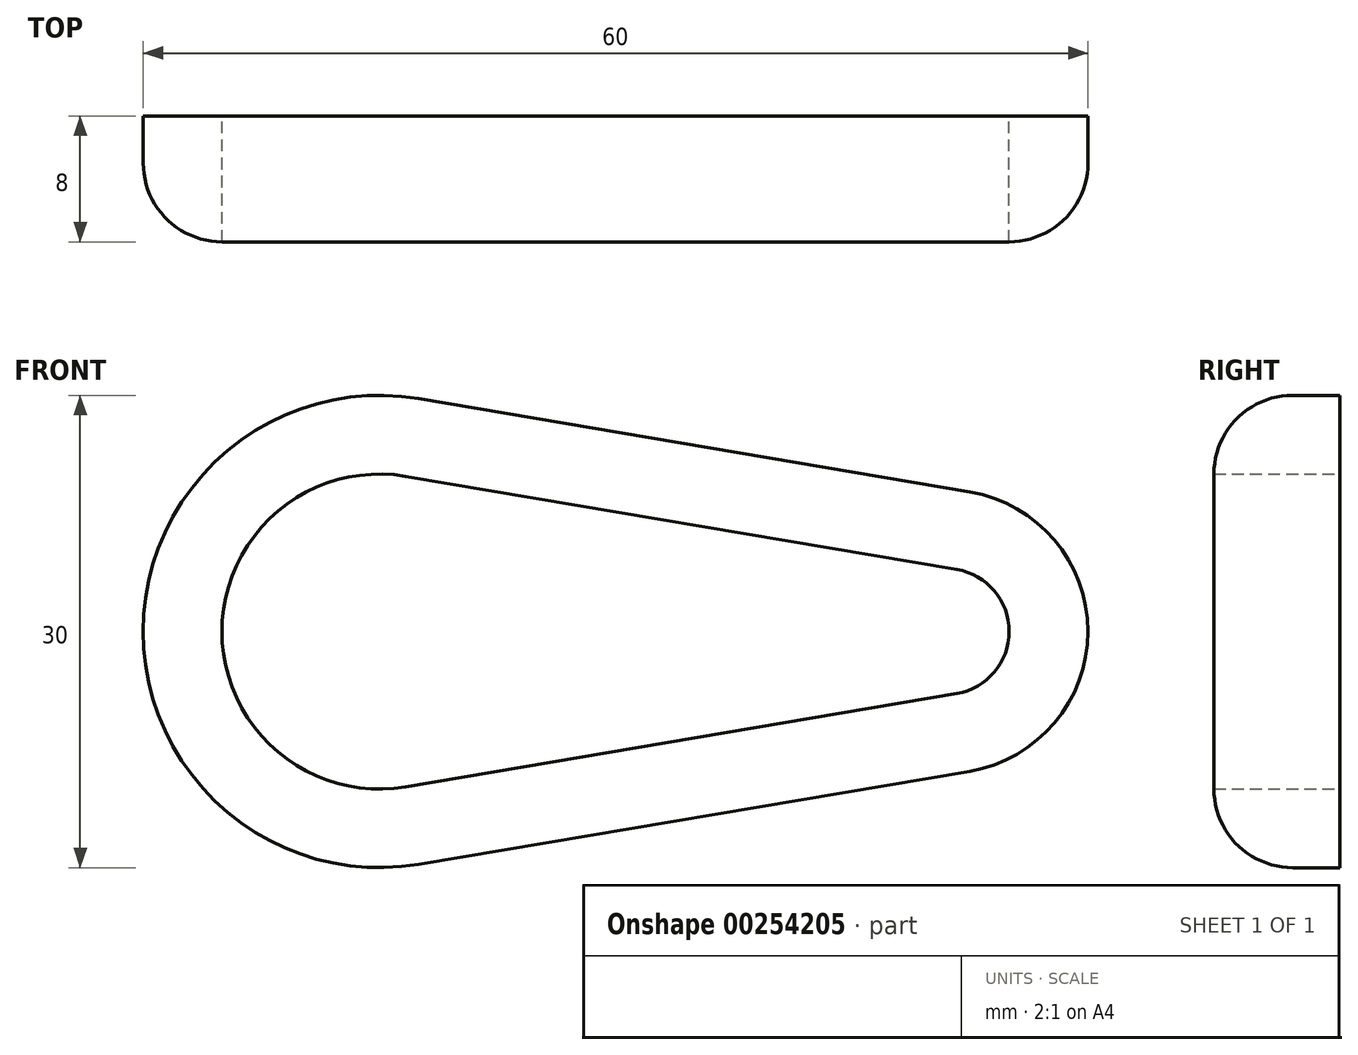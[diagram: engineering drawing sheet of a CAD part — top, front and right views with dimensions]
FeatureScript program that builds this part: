
annotation { "Feature Type Name" : "Feature", "Feature Type Description" : "" }
export const myFeature = defineFeature(function(context is Context, id is Id, definition is map)
    precondition{}
    {
        {
            var Q0;
            Q0=qCreatedBy(makeId("Front.planeOp"),FACE);
            var sketch = newSketch(context, id + "F0", { "sketchPlane" : qUnion([Q0])});
            skCircle(sketch, "E0", {"center": v(-38.66, 0) * mm, "radius": 10 * mm});
            skCircle(sketch, "E1", {"center": v(-2.66, 0) * mm, "radius": 4 * mm});
            skLineSegment(sketch, "E2", {"start": v(-37, 9.86) * mm, "end": v(-2, 3.94) * mm});
            skLineSegment(sketch, "E3", {"start": v(-37, -9.86) * mm, "end": v(-2, -3.94) * mm});
            skCircle(sketch, "E4.0", {"center": v(-38.66, 0) * mm, "radius": 15 * mm});
            skCircle(sketch, "E5.0", {"center": v(-2.66, 0) * mm, "radius": 9 * mm});
            skLineSegment(sketch, "E6", {"start": v(-36.16, 14.8) * mm, "end": v(-1.16, 8.87) * mm});
            skLineSegment(sketch, "E7", {"start": v(-36.16, -14.8) * mm, "end": v(-1.16, -8.87) * mm});
            skSolve(sketch);
        }
        {
            var Q0;
            {var subQ2=sQuery(id+"F0.wireOp",EDGE,"E2");var subQ5=sQuery(id+"F0.wireOp",EDGE,"E0");var subQ8=makeQuery(id+"F0.imprint","INTERSECT",VERTEX,{"derivedFrom":[subQ5,subQ2]});Q0=makeQuery(id+"F0.imprint","IMPRINT",FACE,{"disambiguationData":[TD([[makeQuery(id+"F0.imprint","IMPRINT",EDGE,{"disambiguationData":[TD([[subQ8,-1.0]])],"derivedFrom":subQ5}),-1.0]])]});}
            var Q1;
            {var subQ5=sQuery(id+"F0.wireOp",EDGE,"E6");Q1=makeQuery(id+"F0.imprint","IMPRINT",FACE,{"disambiguationData":[TD([[makeQuery(id+"F0.imprint","IMPRINT",EDGE,{"derivedFrom":subQ5}),-1.0]])]});}
            var Q2;
            {var subQ5=sQuery(id+"F0.wireOp",EDGE,"E7");Q2=makeQuery(id+"F0.imprint","IMPRINT",FACE,{"disambiguationData":[TD([[makeQuery(id+"F0.imprint","IMPRINT",EDGE,{"derivedFrom":subQ5}),1.0]])]});}
            var Q3;
            {var subQ2=sQuery(id+"F0.wireOp",EDGE,"E2");var subQ5=sQuery(id+"F0.wireOp",EDGE,"E1");var subQ8=makeQuery(id+"F0.imprint","INTERSECT",VERTEX,{"derivedFrom":[subQ5,subQ2]});Q3=makeQuery(id+"F0.imprint","IMPRINT",FACE,{"disambiguationData":[TD([[makeQuery(id+"F0.imprint","IMPRINT",EDGE,{"disambiguationData":[TD([[subQ8,1.0]])],"derivedFrom":subQ5}),-1.0]])]});}
            extrude(context, id + "F1", {"entities" : qUnion([Q0, Q1, Q2, Q3]), "depth" : 8 * mm});
        }
        {
            var Q0;
            Q0=makeQuery(id+"F1.opExtrude","CAP_EDGE",EDGE,{"disambiguationData":[OSD([sQuery(id+"F0.wireOp",EDGE,"E6")])],"isStart":false});
            fillet(context, id + "F2", {"entities" : qUnion([Q0]), "radius" : 5 * mm, "tangentPropagation" : true, "allowEdgeOverflow" : false});
        }
    });
